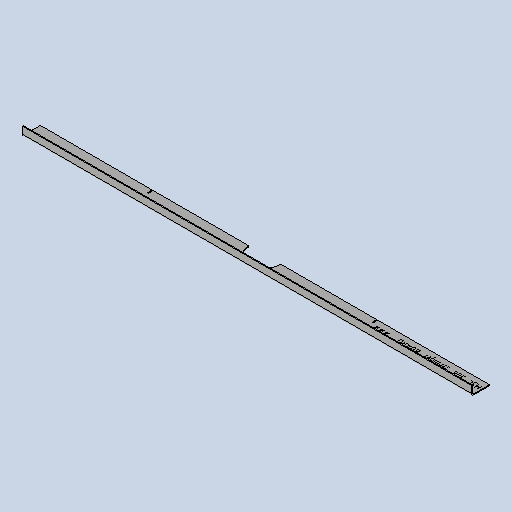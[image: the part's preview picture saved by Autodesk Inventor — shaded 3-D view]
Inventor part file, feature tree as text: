
AUTODESK INVENTOR PART (.ipt)
format: ipt  version: 2025 (Build 290162010, 162A)  size: 310,272 bytes
history: native  units: mm
features: other x5, sheet_metal_op x4, sketch x4, extrude x1
ambient origin geometry x8: Origin, YZ Plane, XZ Plane, XY Plane, X Axis, Y Axis, Z Axis, Center Point
bodies: Solid1 (feature_tree)
feature tree (14):
  sheet_metal_op  "Face1"
  sheet_metal_op  "Flange1"
  extrude  "Extrusion1"  Depth=39.0mm
  other  "Mark2"
  other  "A-Side Definition"
  sketch  "Sketch1"  dims[d0=980.0mm d1=39.0mm]
  other  "Plate1"
  sketch  "Sketch2"  dims[d2=2.0mm]
  other  "Plate2"
  sheet_metal_op  "Bend1"
  sheet_metal_op  "Corner1"
  sketch  "Sketch5"  dims[d3=2.0mm]
  sketch  "Sketch9"  dims[d4=1.0mm d5=4.0mm d6=2.75mm d7=20.0mm d8=90.0deg d9=2.75mm d10=8.0mm d11=2.0mm d12=2.75mm d15=0.0mm d16=0.0mm d40=200.0mm d41=12.0mm d45=70.0mm d48=2.1mm d49=490.0mm d51=29.0mm d52=10.0mm]
  other  "Definition1"
